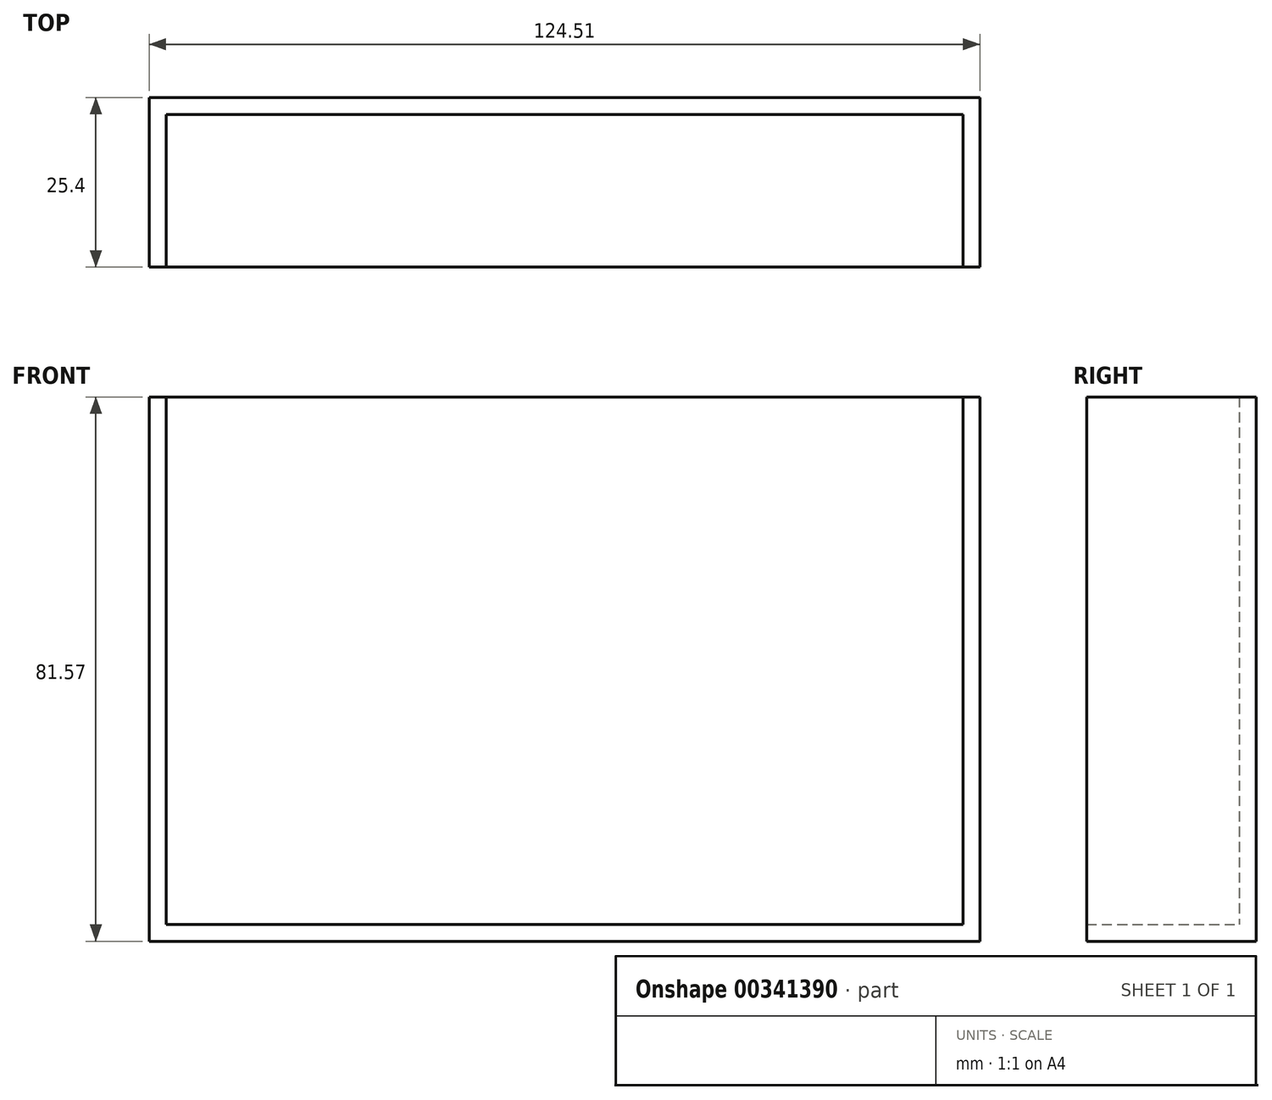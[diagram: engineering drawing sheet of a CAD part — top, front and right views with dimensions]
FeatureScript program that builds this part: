
annotation { "Feature Type Name" : "Feature", "Feature Type Description" : "" }
export const myFeature = defineFeature(function(context is Context, id is Id, definition is map)
    precondition{}
    {
        {
            var Q0;
            Q0=qCreatedBy(makeId("Front.planeOp"),FACE);
            var sketch = newSketch(context, id + "F0", { "sketchPlane" : qUnion([Q0])});
            skLineSegment(sketch, "E0.bottom", {"start": v(-35.73, 57.28) * mm, "end": v(88.78, 57.28) * mm});
            skLineSegment(sketch, "E0.top", {"start": v(-35.73, -24.29) * mm, "end": v(88.78, -24.29) * mm});
            skLineSegment(sketch, "E0.left", {"start": v(-35.73, 57.28) * mm, "end": v(-35.73, -24.29) * mm});
            skLineSegment(sketch, "E0.right", {"start": v(88.78, 57.28) * mm, "end": v(88.78, -24.29) * mm});
            skSolve(sketch);
        }
        {
            var Q0;
            Q0=makeQuery(id+"F0.imprint","IMPRINT",FACE,{"disambiguationData":[TD([[makeQuery(id+"F0.imprint","IMPRINT",EDGE,{"derivedFrom":sQuery(id+"F0.wireOp",EDGE,"E0.bottom")}),-1.0]])]});
            extrude(context, id + "F1", {"entities" : qUnion([Q0]), "depth" : 25.4 * mm});
        }
        {
            var Q0;
            Q0=makeQuery(id+"F1.opExtrude","SWEPT_FACE",FACE,{"disambiguationData":[OSD([sQuery(id+"F0.wireOp",EDGE,"E0.bottom")])]});
            var Q1;
            Q1=makeQuery(id+"F1.opExtrude","CAP_FACE",FACE,{"disambiguationData":[OSD([sQuery(id+"F0.wireOp",EDGE,"E0.bottom"),sQuery(id+"F0.wireOp",EDGE,"E0.top"),sQuery(id+"F0.wireOp",EDGE,"E0.left"),sQuery(id+"F0.wireOp",EDGE,"E0.right")])],"isStart":false});
            shell(context, id + "F2", {"entities" : qUnion([Q0, Q1]), "thickness" : 2.54 * mm});
        }
    });
